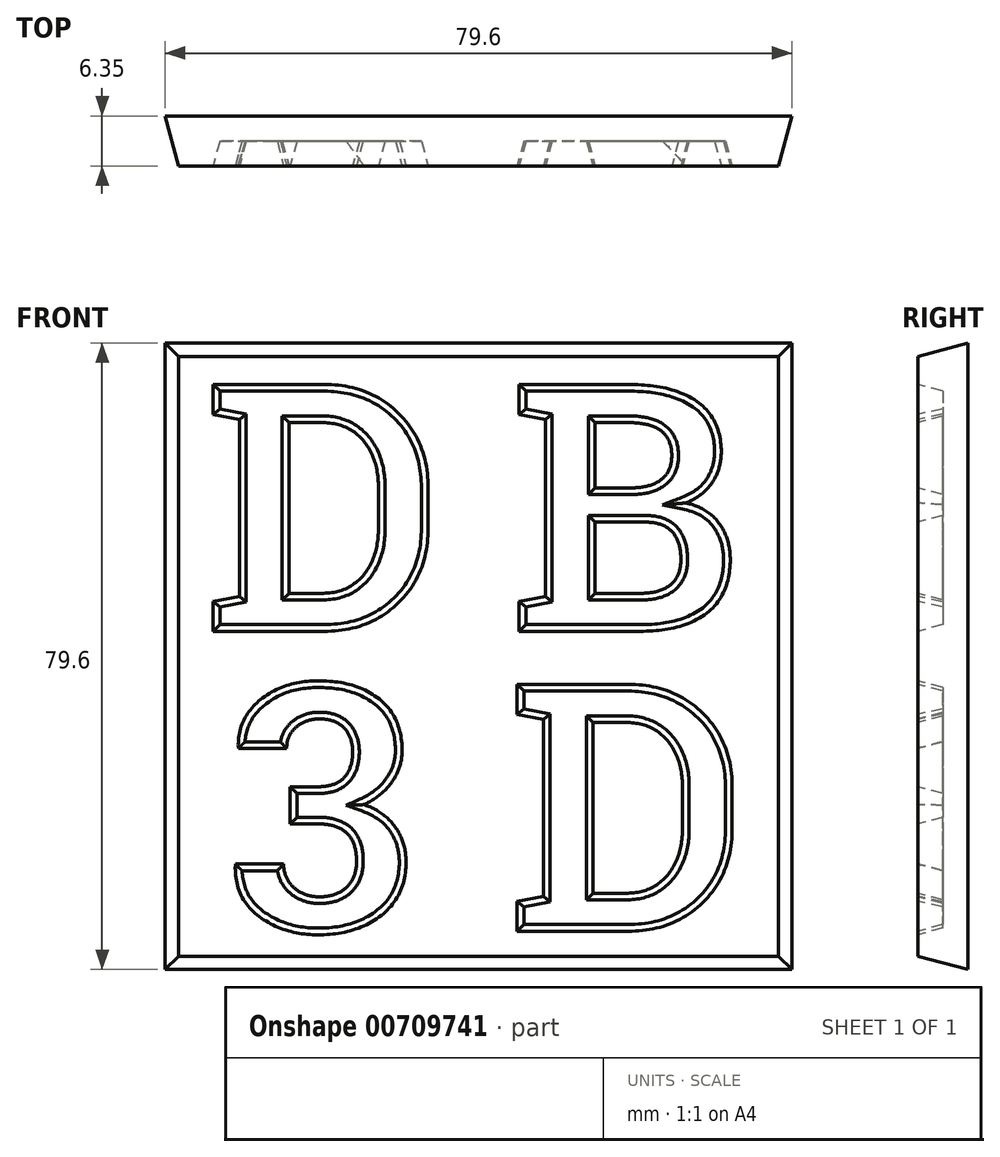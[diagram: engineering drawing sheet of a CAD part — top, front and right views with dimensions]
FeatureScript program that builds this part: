
annotation { "Feature Type Name" : "Feature", "Feature Type Description" : "" }
export const myFeature = defineFeature(function(context is Context, id is Id, definition is map)
    precondition{}
    {
        {
            var Q0;
            Q0=qCreatedBy(makeId("Front.planeOp"),FACE);
            var sketch = newSketch(context, id + "F0", { "sketchPlane" : qUnion([Q0])});
            skLineSegment(sketch, "E0.bottom", {"start": v(38.1, 38.1) * mm, "end": v(-38.1, 38.1) * mm});
            skLineSegment(sketch, "E0.top", {"start": v(38.1, -38.1) * mm, "end": v(-38.1, -38.1) * mm});
            skLineSegment(sketch, "E0.left", {"start": v(38.1, 38.1) * mm, "end": v(38.1, -38.1) * mm});
            skLineSegment(sketch, "E0.right", {"start": v(-38.1, 38.1) * mm, "end": v(-38.1, -38.1) * mm});
            skPoint(sketch, "E0.middle", {"position": v(0, 0) * mm});
            skSolve(sketch);
        }
        {
            var Q0;
            Q0=makeQuery(id+"F0.imprint","IMPRINT",FACE,{"disambiguationData":[TD([[makeQuery(id+"F0.imprint","IMPRINT",EDGE,{"derivedFrom":sQuery(id+"F0.wireOp",EDGE,"E0.bottom")}),1.0]])]});
            extrude(context, id + "F1", {"entities" : qUnion([Q0]), "oppositeDirection" : true, "depth" : 6.35 * mm, "offsetDistance" : 25.4 * mm, "hasDraft" : true, "draftAngle" : 15 * degree});
        }
        {
            var Q0;
            Q0=makeQuery(id+"F1.opExtrude","CAP_FACE",FACE,{"disambiguationData":[OSD([sQuery(id+"F0.wireOp",EDGE,"E0.bottom"),sQuery(id+"F0.wireOp",EDGE,"E0.top"),sQuery(id+"F0.wireOp",EDGE,"E0.left"),sQuery(id+"F0.wireOp",EDGE,"E0.right")])],"isStart":true});
            var sketch = newSketch(context, id + "F2", { "sketchPlane" : qUnion([Q0])});
            skLineSegment(sketch, "E1", {"start": v(-38.1, 0) * mm, "end": v(39.95, 0) * mm, "construction": true});
            skPoint(sketch, "E1.endSnap0", {"position": v(38.1, 0) * mm});
            skLineSegment(sketch, "E2", {"start": v(0, -38.1) * mm, "end": v(0, 38.1) * mm, "construction": true});
            skText(sketch, "E3", { "text": "D", "fontName": "RobotoSlab-Bold.ttf"});
            skText(sketch, "E4", { "text": "D", "fontName": "RobotoSlab-Bold.ttf"});
            skText(sketch, "E5", { "text": "B", "fontName": "RobotoSlab-Bold.ttf"});
            skText(sketch, "E6", { "text": "3", "fontName": "RobotoSlab-Bold.ttf"});
            const initialGuessF2  = {"E3": [-0.03492, 0.00318, 1, 0, 0.03175], "E4": [0.00371, -0.03492, 1, 0, 0.03175], "E5": [0.00396, 0.00318, 1, 0, 0.03175], "E6": [-0.03212, -0.03492, 1, 0, 0.03175]};
            skSetInitialGuess(sketch, initialGuessF2);
            skSolve(sketch);
        }
        {
            var Q0;
            Q0 = qSketchRegion(id + "F2", true);
            extrude(context, id + "F3", {"entities" : qUnion([Q0]), "operationType" : NewBodyOperationType.REMOVE, "oppositeDirection" : true, "depth" : 3.17 * mm, "offsetDistance" : 25.4 * mm, "hasDraft" : true, "draftAngle" : 15 * degree, "draftPullDirection" : true});
        }
    });
